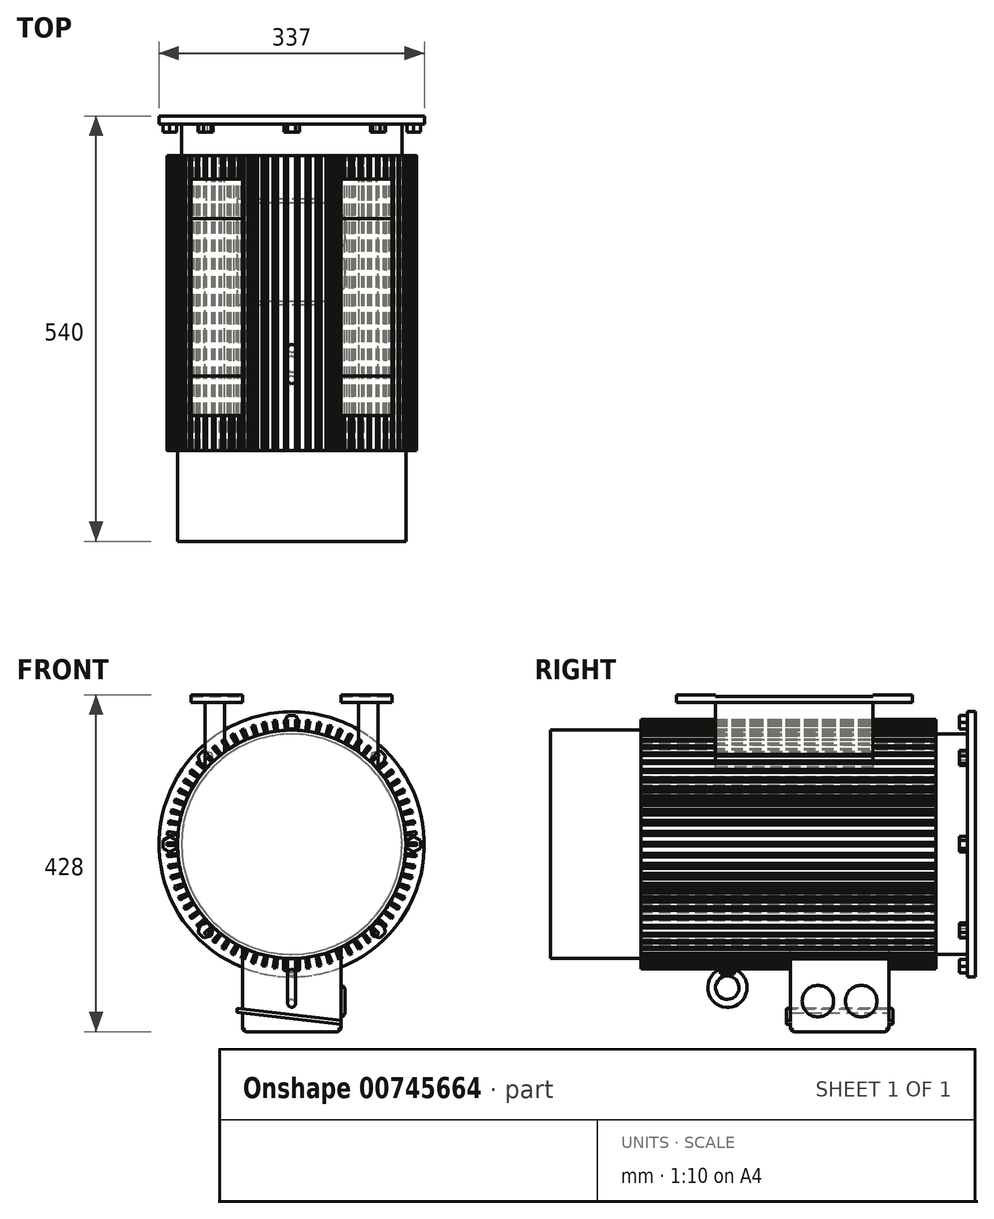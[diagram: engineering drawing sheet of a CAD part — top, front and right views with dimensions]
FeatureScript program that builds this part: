
annotation { "Feature Type Name" : "Feature", "Feature Type Description" : "" }
export const myFeature = defineFeature(function(context is Context, id is Id, definition is map)
    precondition{}
    {
        {
            var Q0;
            Q0=qCreatedBy(makeId("Front.planeOp"),FACE);
            var sketch = newSketch(context, id + "F0", { "sketchPlane" : qUnion([Q0])});
            skCircle(sketch, "E0", {"center": v(0, 0) * mm, "radius": 158.5 * mm});
            skSolve(sketch);
        }
        {
            var Q0;
            Q0=makeQuery(id+"F0.imprint","IMPRINT",FACE,{"disambiguationData":[TD([[makeQuery(id+"F0.imprint","IMPRINT",EDGE,{"derivedFrom":sQuery(id+"F0.wireOp",EDGE,"E0")}),1.0]])]});
            extrude(context, id + "F1", {"entities" : qUnion([Q0]), "depth" : 500 * mm, "offsetDistance" : 25 * mm});
        }
        {
            var Q0;
            Q0=makeQuery(id+"F1.opExtrude","CAP_FACE",FACE,{"disambiguationData":[OSD([sQuery(id+"F0.wireOp",EDGE,"E0")])],"isStart":false});
            var sketch = newSketch(context, id + "F2", { "sketchPlane" : qUnion([Q0])});
            skCircle(sketch, "E1", {"center": v(0, 0) * mm, "radius": 145 * mm});
            skSolve(sketch);
        }
        {
            var Q0;
            Q0=makeQuery(id+"F2.imprint","IMPRINT",FACE,{"disambiguationData":[TD([[makeQuery(id+"F2.imprint","IMPRINT",EDGE,{"derivedFrom":sQuery(id+"F2.wireOp",EDGE,"E1")}),-1.0]])]});
            extrude(context, id + "F3", {"entities" : qUnion([Q0]), "operationType" : NewBodyOperationType.REMOVE, "oppositeDirection" : true, "depth" : 125 * mm, "offsetDistance" : 25 * mm});
        }
        {
            var Q0;
            Q0=makeQuery(id+"F1.opExtrude","CAP_FACE",FACE,{"disambiguationData":[OSD([sQuery(id+"F0.wireOp",EDGE,"E0")])],"isStart":false});
            extrude(context, id + "F4", {"entities" : qUnion([Q0]), "operationType" : NewBodyOperationType.REMOVE, "oppositeDirection" : true, "depth" : 10 * mm, "offsetDistance" : 25 * mm});
        }
        {
            var Q0;
            Q0=makeQuery(id+"F1.opExtrude","CAP_FACE",FACE,{"disambiguationData":[OSD([sQuery(id+"F0.wireOp",EDGE,"E0")])],"isStart":true});
            var sketch = newSketch(context, id + "F5", { "sketchPlane" : qUnion([Q0])});
            skLineSegment(sketch, "E2.bottom", {"start": v(-5, 175) * mm, "end": v(5, 175) * mm});
            skLineSegment(sketch, "E2.top", {"start": v(-5, 145) * mm, "end": v(5, 145) * mm});
            skLineSegment(sketch, "E2.left", {"start": v(-5, 175) * mm, "end": v(-5, 145) * mm});
            skLineSegment(sketch, "E2.right", {"start": v(5, 175) * mm, "end": v(5, 145) * mm});
            skLineSegment(sketch, "E3.1.0", {"start": v(-10.7, 174.74) * mm, "end": v(-8.02, 144.86) * mm});
            skLineSegment(sketch, "E3.1.1", {"start": v(-20.67, 173.85) * mm, "end": v(-17.98, 143.97) * mm});
            skLineSegment(sketch, "E3.1.2", {"start": v(-17.98, 143.97) * mm, "end": v(-8.02, 144.86) * mm});
            skLineSegment(sketch, "E3.1.3", {"start": v(-20.67, 173.85) * mm, "end": v(-10.7, 174.74) * mm});
            skLineSegment(sketch, "E3.2.0", {"start": v(-26.33, 173.08) * mm, "end": v(-20.97, 143.56) * mm});
            skLineSegment(sketch, "E3.2.1", {"start": v(-36.17, 171.3) * mm, "end": v(-30.81, 141.78) * mm});
            skLineSegment(sketch, "E3.2.2", {"start": v(-30.81, 141.78) * mm, "end": v(-20.97, 143.56) * mm});
            skLineSegment(sketch, "E3.2.3", {"start": v(-36.17, 171.3) * mm, "end": v(-26.33, 173.08) * mm});
            skLineSegment(sketch, "E3.3.0", {"start": v(-41.74, 170.02) * mm, "end": v(-33.76, 141.1) * mm});
            skLineSegment(sketch, "E3.3.1", {"start": v(-51.38, 167.36) * mm, "end": v(-43.4, 138.44) * mm});
            skLineSegment(sketch, "E3.3.2", {"start": v(-43.4, 138.44) * mm, "end": v(-33.76, 141.1) * mm});
            skLineSegment(sketch, "E3.3.3", {"start": v(-51.38, 167.36) * mm, "end": v(-41.74, 170.02) * mm});
            skLineSegment(sketch, "E3.4.0", {"start": v(-56.8, 165.6) * mm, "end": v(-46.27, 137.51) * mm});
            skLineSegment(sketch, "E3.4.1", {"start": v(-66.17, 162.08) * mm, "end": v(-55.63, 134) * mm});
            skLineSegment(sketch, "E3.4.2", {"start": v(-55.63, 134) * mm, "end": v(-46.27, 137.51) * mm});
            skLineSegment(sketch, "E3.4.3", {"start": v(-66.17, 162.08) * mm, "end": v(-56.8, 165.6) * mm});
            skLineSegment(sketch, "E3.5.0", {"start": v(-71.42, 159.84) * mm, "end": v(-58.4, 132.8) * mm});
            skLineSegment(sketch, "E3.5.1", {"start": v(-80.43, 155.5) * mm, "end": v(-67.42, 128.47) * mm});
            skLineSegment(sketch, "E3.5.2", {"start": v(-67.42, 128.47) * mm, "end": v(-58.4, 132.8) * mm});
            skLineSegment(sketch, "E3.5.3", {"start": v(-80.43, 155.5) * mm, "end": v(-71.42, 159.84) * mm});
            skLineSegment(sketch, "E3.6.0", {"start": v(-85.47, 152.8) * mm, "end": v(-70.08, 127.04) * mm});
            skLineSegment(sketch, "E3.6.1", {"start": v(-94.05, 147.66) * mm, "end": v(-78.66, 121.91) * mm});
            skLineSegment(sketch, "E3.6.2", {"start": v(-78.66, 121.91) * mm, "end": v(-70.08, 127.04) * mm});
            skLineSegment(sketch, "E3.6.3", {"start": v(-94.05, 147.66) * mm, "end": v(-85.47, 152.8) * mm});
            skLineSegment(sketch, "E3.7.0", {"start": v(-98.82, 144.52) * mm, "end": v(-81.18, 120.25) * mm});
            skLineSegment(sketch, "E3.7.1", {"start": v(-106.9, 138.64) * mm, "end": v(-89.27, 114.37) * mm});
            skLineSegment(sketch, "E3.7.2", {"start": v(-89.27, 114.37) * mm, "end": v(-81.18, 120.25) * mm});
            skLineSegment(sketch, "E3.7.3", {"start": v(-106.9, 138.64) * mm, "end": v(-98.82, 144.52) * mm});
            skLineSegment(sketch, "E3.8.0", {"start": v(-111.37, 135.08) * mm, "end": v(-91.64, 112.49) * mm});
            skLineSegment(sketch, "E3.8.1", {"start": v(-118.9, 128.5) * mm, "end": v(-99.17, 105.9) * mm});
            skLineSegment(sketch, "E3.8.2", {"start": v(-99.17, 105.9) * mm, "end": v(-91.64, 112.49) * mm});
            skLineSegment(sketch, "E3.8.3", {"start": v(-118.9, 128.5) * mm, "end": v(-111.37, 135.08) * mm});
            skLineSegment(sketch, "E3.9.0", {"start": v(-123.03, 124.55) * mm, "end": v(-101.35, 103.82) * mm});
            skLineSegment(sketch, "E3.9.1", {"start": v(-129.94, 117.32) * mm, "end": v(-108.26, 96.6) * mm});
            skLineSegment(sketch, "E3.9.2", {"start": v(-108.26, 96.6) * mm, "end": v(-101.35, 103.82) * mm});
            skLineSegment(sketch, "E3.9.3", {"start": v(-129.94, 117.32) * mm, "end": v(-123.03, 124.55) * mm});
            skLineSegment(sketch, "E3.10.0", {"start": v(-133.7, 113.02) * mm, "end": v(-110.25, 94.32) * mm});
            skLineSegment(sketch, "E3.10.1", {"start": v(-139.94, 105.2) * mm, "end": v(-116.48, 86.5) * mm});
            skLineSegment(sketch, "E3.10.2", {"start": v(-116.48, 86.5) * mm, "end": v(-110.25, 94.32) * mm});
            skLineSegment(sketch, "E3.10.3", {"start": v(-139.94, 105.2) * mm, "end": v(-133.7, 113.02) * mm});
            skLineSegment(sketch, "E3.11.0", {"start": v(-143.3, 100.58) * mm, "end": v(-118.26, 84.05) * mm});
            skLineSegment(sketch, "E3.11.1", {"start": v(-148.8, 92.23) * mm, "end": v(-123.77, 75.7) * mm});
            skLineSegment(sketch, "E3.11.2", {"start": v(-123.77, 75.7) * mm, "end": v(-118.26, 84.05) * mm});
            skLineSegment(sketch, "E3.11.3", {"start": v(-148.8, 92.23) * mm, "end": v(-143.3, 100.58) * mm});
            skLineSegment(sketch, "E3.12.0", {"start": v(-151.73, 87.33) * mm, "end": v(-125.32, 73.11) * mm});
            skLineSegment(sketch, "E3.12.1", {"start": v(-156.47, 78.52) * mm, "end": v(-130.06, 64.3) * mm});
            skLineSegment(sketch, "E3.12.2", {"start": v(-130.06, 64.3) * mm, "end": v(-125.32, 73.11) * mm});
            skLineSegment(sketch, "E3.12.3", {"start": v(-156.47, 78.52) * mm, "end": v(-151.73, 87.33) * mm});
            skLineSegment(sketch, "E3.13.0", {"start": v(-158.95, 73.38) * mm, "end": v(-131.37, 61.59) * mm});
            skLineSegment(sketch, "E3.13.1", {"start": v(-162.88, 64.18) * mm, "end": v(-135.3, 52.4) * mm});
            skLineSegment(sketch, "E3.13.2", {"start": v(-135.3, 52.4) * mm, "end": v(-131.37, 61.59) * mm});
            skLineSegment(sketch, "E3.13.3", {"start": v(-162.88, 64.18) * mm, "end": v(-158.95, 73.38) * mm});
            skLineSegment(sketch, "E3.14.0", {"start": v(-164.89, 58.83) * mm, "end": v(-136.36, 49.56) * mm});
            skLineSegment(sketch, "E3.14.1", {"start": v(-167.98, 49.32) * mm, "end": v(-139.45, 40.05) * mm});
            skLineSegment(sketch, "E3.14.2", {"start": v(-139.45, 40.05) * mm, "end": v(-136.36, 49.56) * mm});
            skLineSegment(sketch, "E3.14.3", {"start": v(-167.98, 49.32) * mm, "end": v(-164.89, 58.83) * mm});
            skLineSegment(sketch, "E3.15.0", {"start": v(-169.5, 43.82) * mm, "end": v(-140.25, 37.14) * mm});
            skLineSegment(sketch, "E3.15.1", {"start": v(-171.72, 34.07) * mm, "end": v(-142.48, 27.4) * mm});
            skLineSegment(sketch, "E3.15.2", {"start": v(-142.48, 27.4) * mm, "end": v(-140.25, 37.14) * mm});
            skLineSegment(sketch, "E3.15.3", {"start": v(-171.72, 34.07) * mm, "end": v(-169.5, 43.82) * mm});
            skLineSegment(sketch, "E3.16.0", {"start": v(-172.75, 28.45) * mm, "end": v(-143.02, 24.42) * mm});
            skLineSegment(sketch, "E3.16.1", {"start": v(-174.09, 18.54) * mm, "end": v(-144.36, 14.5) * mm});
            skLineSegment(sketch, "E3.16.2", {"start": v(-144.36, 14.5) * mm, "end": v(-143.02, 24.42) * mm});
            skLineSegment(sketch, "E3.16.3", {"start": v(-174.09, 18.54) * mm, "end": v(-172.75, 28.45) * mm});
            skLineSegment(sketch, "E3.17.0", {"start": v(-174.6, 12.85) * mm, "end": v(-144.63, 11.5) * mm});
            skLineSegment(sketch, "E3.17.1", {"start": v(-175.05, 2.86) * mm, "end": v(-145.08, 1.51) * mm});
            skLineSegment(sketch, "E3.17.2", {"start": v(-145.08, 1.51) * mm, "end": v(-144.63, 11.5) * mm});
            skLineSegment(sketch, "E3.17.3", {"start": v(-175.05, 2.86) * mm, "end": v(-174.6, 12.85) * mm});
            skLineSegment(sketch, "E3.18.0", {"start": v(-175.05, -2.86) * mm, "end": v(-145.08, -1.51) * mm});
            skLineSegment(sketch, "E3.18.1", {"start": v(-174.6, -12.85) * mm, "end": v(-144.63, -11.5) * mm});
            skLineSegment(sketch, "E3.18.2", {"start": v(-144.63, -11.5) * mm, "end": v(-145.08, -1.51) * mm});
            skLineSegment(sketch, "E3.18.3", {"start": v(-174.6, -12.85) * mm, "end": v(-175.05, -2.86) * mm});
            skLineSegment(sketch, "E3.19.0", {"start": v(-174.09, -18.54) * mm, "end": v(-144.36, -14.5) * mm});
            skLineSegment(sketch, "E3.19.1", {"start": v(-172.75, -28.45) * mm, "end": v(-143.02, -24.42) * mm});
            skLineSegment(sketch, "E3.19.2", {"start": v(-143.02, -24.42) * mm, "end": v(-144.36, -14.5) * mm});
            skLineSegment(sketch, "E3.19.3", {"start": v(-172.75, -28.45) * mm, "end": v(-174.09, -18.54) * mm});
            skLineSegment(sketch, "E3.20.0", {"start": v(-171.72, -34.07) * mm, "end": v(-142.48, -27.4) * mm});
            skLineSegment(sketch, "E3.20.1", {"start": v(-169.5, -43.82) * mm, "end": v(-140.25, -37.14) * mm});
            skLineSegment(sketch, "E3.20.2", {"start": v(-140.25, -37.14) * mm, "end": v(-142.48, -27.4) * mm});
            skLineSegment(sketch, "E3.20.3", {"start": v(-169.5, -43.82) * mm, "end": v(-171.72, -34.07) * mm});
            skLineSegment(sketch, "E3.21.0", {"start": v(-167.98, -49.32) * mm, "end": v(-139.45, -40.05) * mm});
            skLineSegment(sketch, "E3.21.1", {"start": v(-164.89, -58.83) * mm, "end": v(-136.36, -49.56) * mm});
            skLineSegment(sketch, "E3.21.2", {"start": v(-136.36, -49.56) * mm, "end": v(-139.45, -40.05) * mm});
            skLineSegment(sketch, "E3.21.3", {"start": v(-164.89, -58.83) * mm, "end": v(-167.98, -49.32) * mm});
            skLineSegment(sketch, "E3.22.0", {"start": v(-162.88, -64.18) * mm, "end": v(-135.3, -52.4) * mm});
            skLineSegment(sketch, "E3.22.1", {"start": v(-158.95, -73.38) * mm, "end": v(-131.37, -61.59) * mm});
            skLineSegment(sketch, "E3.22.2", {"start": v(-131.37, -61.59) * mm, "end": v(-135.3, -52.4) * mm});
            skLineSegment(sketch, "E3.22.3", {"start": v(-158.95, -73.38) * mm, "end": v(-162.88, -64.18) * mm});
            skLineSegment(sketch, "E3.23.0", {"start": v(-156.47, -78.52) * mm, "end": v(-130.06, -64.3) * mm});
            skLineSegment(sketch, "E3.23.1", {"start": v(-151.73, -87.33) * mm, "end": v(-125.32, -73.11) * mm});
            skLineSegment(sketch, "E3.23.2", {"start": v(-125.32, -73.11) * mm, "end": v(-130.06, -64.3) * mm});
            skLineSegment(sketch, "E3.23.3", {"start": v(-151.73, -87.33) * mm, "end": v(-156.47, -78.52) * mm});
            skLineSegment(sketch, "E3.24.0", {"start": v(-148.8, -92.23) * mm, "end": v(-123.77, -75.7) * mm});
            skLineSegment(sketch, "E3.24.1", {"start": v(-143.3, -100.58) * mm, "end": v(-118.26, -84.05) * mm});
            skLineSegment(sketch, "E3.24.2", {"start": v(-118.26, -84.05) * mm, "end": v(-123.77, -75.7) * mm});
            skLineSegment(sketch, "E3.24.3", {"start": v(-143.3, -100.58) * mm, "end": v(-148.8, -92.23) * mm});
            skLineSegment(sketch, "E3.25.0", {"start": v(-139.94, -105.2) * mm, "end": v(-116.48, -86.5) * mm});
            skLineSegment(sketch, "E3.25.1", {"start": v(-133.7, -113.02) * mm, "end": v(-110.25, -94.32) * mm});
            skLineSegment(sketch, "E3.25.2", {"start": v(-110.25, -94.32) * mm, "end": v(-116.48, -86.5) * mm});
            skLineSegment(sketch, "E3.25.3", {"start": v(-133.7, -113.02) * mm, "end": v(-139.94, -105.2) * mm});
            skLineSegment(sketch, "E3.26.0", {"start": v(-129.94, -117.32) * mm, "end": v(-108.26, -96.6) * mm});
            skLineSegment(sketch, "E3.26.1", {"start": v(-123.03, -124.55) * mm, "end": v(-101.35, -103.82) * mm});
            skLineSegment(sketch, "E3.26.2", {"start": v(-101.35, -103.82) * mm, "end": v(-108.26, -96.6) * mm});
            skLineSegment(sketch, "E3.26.3", {"start": v(-123.03, -124.55) * mm, "end": v(-129.94, -117.32) * mm});
            skLineSegment(sketch, "E3.27.0", {"start": v(-118.9, -128.5) * mm, "end": v(-99.17, -105.9) * mm});
            skLineSegment(sketch, "E3.27.1", {"start": v(-111.37, -135.08) * mm, "end": v(-91.64, -112.49) * mm});
            skLineSegment(sketch, "E3.27.2", {"start": v(-91.64, -112.49) * mm, "end": v(-99.17, -105.9) * mm});
            skLineSegment(sketch, "E3.27.3", {"start": v(-111.37, -135.08) * mm, "end": v(-118.9, -128.5) * mm});
            skLineSegment(sketch, "E3.28.0", {"start": v(-106.9, -138.64) * mm, "end": v(-89.27, -114.37) * mm});
            skLineSegment(sketch, "E3.28.1", {"start": v(-98.82, -144.52) * mm, "end": v(-81.18, -120.25) * mm});
            skLineSegment(sketch, "E3.28.2", {"start": v(-81.18, -120.25) * mm, "end": v(-89.27, -114.37) * mm});
            skLineSegment(sketch, "E3.28.3", {"start": v(-98.82, -144.52) * mm, "end": v(-106.9, -138.64) * mm});
            skLineSegment(sketch, "E3.29.0", {"start": v(-94.05, -147.66) * mm, "end": v(-78.66, -121.91) * mm});
            skLineSegment(sketch, "E3.29.1", {"start": v(-85.47, -152.8) * mm, "end": v(-70.08, -127.04) * mm});
            skLineSegment(sketch, "E3.29.2", {"start": v(-70.08, -127.04) * mm, "end": v(-78.66, -121.91) * mm});
            skLineSegment(sketch, "E3.29.3", {"start": v(-85.47, -152.8) * mm, "end": v(-94.05, -147.66) * mm});
            skLineSegment(sketch, "E3.30.0", {"start": v(-80.43, -155.5) * mm, "end": v(-67.42, -128.47) * mm});
            skLineSegment(sketch, "E3.30.1", {"start": v(-71.42, -159.84) * mm, "end": v(-58.4, -132.8) * mm});
            skLineSegment(sketch, "E3.30.2", {"start": v(-58.4, -132.8) * mm, "end": v(-67.42, -128.47) * mm});
            skLineSegment(sketch, "E3.30.3", {"start": v(-71.42, -159.84) * mm, "end": v(-80.43, -155.5) * mm});
            skLineSegment(sketch, "E3.31.0", {"start": v(-66.17, -162.08) * mm, "end": v(-55.63, -134) * mm});
            skLineSegment(sketch, "E3.31.1", {"start": v(-56.8, -165.6) * mm, "end": v(-46.27, -137.51) * mm});
            skLineSegment(sketch, "E3.31.2", {"start": v(-46.27, -137.51) * mm, "end": v(-55.63, -134) * mm});
            skLineSegment(sketch, "E3.31.3", {"start": v(-56.8, -165.6) * mm, "end": v(-66.17, -162.08) * mm});
            skLineSegment(sketch, "E3.32.0", {"start": v(-51.38, -167.36) * mm, "end": v(-43.4, -138.44) * mm});
            skLineSegment(sketch, "E3.32.1", {"start": v(-41.74, -170.02) * mm, "end": v(-33.76, -141.1) * mm});
            skLineSegment(sketch, "E3.32.2", {"start": v(-33.76, -141.1) * mm, "end": v(-43.4, -138.44) * mm});
            skLineSegment(sketch, "E3.32.3", {"start": v(-41.74, -170.02) * mm, "end": v(-51.38, -167.36) * mm});
            skLineSegment(sketch, "E3.33.0", {"start": v(-36.17, -171.3) * mm, "end": v(-30.81, -141.78) * mm});
            skLineSegment(sketch, "E3.33.1", {"start": v(-26.33, -173.08) * mm, "end": v(-20.97, -143.56) * mm});
            skLineSegment(sketch, "E3.33.2", {"start": v(-20.97, -143.56) * mm, "end": v(-30.81, -141.78) * mm});
            skLineSegment(sketch, "E3.33.3", {"start": v(-26.33, -173.08) * mm, "end": v(-36.17, -171.3) * mm});
            skLineSegment(sketch, "E3.34.0", {"start": v(-20.67, -173.85) * mm, "end": v(-17.98, -143.97) * mm});
            skLineSegment(sketch, "E3.34.1", {"start": v(-10.7, -174.74) * mm, "end": v(-8.02, -144.86) * mm});
            skLineSegment(sketch, "E3.34.2", {"start": v(-8.02, -144.86) * mm, "end": v(-17.98, -143.97) * mm});
            skLineSegment(sketch, "E3.34.3", {"start": v(-10.7, -174.74) * mm, "end": v(-20.67, -173.85) * mm});
            skLineSegment(sketch, "E3.35.0", {"start": v(-5, -175) * mm, "end": v(-5, -145) * mm});
            skLineSegment(sketch, "E3.35.1", {"start": v(5, -175) * mm, "end": v(5, -145) * mm});
            skLineSegment(sketch, "E3.35.2", {"start": v(5, -145) * mm, "end": v(-5, -145) * mm});
            skLineSegment(sketch, "E3.35.3", {"start": v(5, -175) * mm, "end": v(-5, -175) * mm});
            skLineSegment(sketch, "E3.36.0", {"start": v(10.7, -174.74) * mm, "end": v(8.02, -144.86) * mm});
            skLineSegment(sketch, "E3.36.1", {"start": v(20.67, -173.85) * mm, "end": v(17.98, -143.97) * mm});
            skLineSegment(sketch, "E3.36.2", {"start": v(17.98, -143.97) * mm, "end": v(8.02, -144.86) * mm});
            skLineSegment(sketch, "E3.36.3", {"start": v(20.67, -173.85) * mm, "end": v(10.7, -174.74) * mm});
            skLineSegment(sketch, "E3.37.0", {"start": v(26.33, -173.08) * mm, "end": v(20.97, -143.56) * mm});
            skLineSegment(sketch, "E3.37.1", {"start": v(36.17, -171.3) * mm, "end": v(30.81, -141.78) * mm});
            skLineSegment(sketch, "E3.37.2", {"start": v(30.81, -141.78) * mm, "end": v(20.97, -143.56) * mm});
            skLineSegment(sketch, "E3.37.3", {"start": v(36.17, -171.3) * mm, "end": v(26.33, -173.08) * mm});
            skLineSegment(sketch, "E3.38.0", {"start": v(41.74, -170.02) * mm, "end": v(33.76, -141.1) * mm});
            skLineSegment(sketch, "E3.38.1", {"start": v(51.38, -167.36) * mm, "end": v(43.4, -138.44) * mm});
            skLineSegment(sketch, "E3.38.2", {"start": v(43.4, -138.44) * mm, "end": v(33.76, -141.1) * mm});
            skLineSegment(sketch, "E3.38.3", {"start": v(51.38, -167.36) * mm, "end": v(41.74, -170.02) * mm});
            skLineSegment(sketch, "E3.39.0", {"start": v(56.8, -165.6) * mm, "end": v(46.27, -137.51) * mm});
            skLineSegment(sketch, "E3.39.1", {"start": v(66.17, -162.08) * mm, "end": v(55.63, -134) * mm});
            skLineSegment(sketch, "E3.39.2", {"start": v(55.63, -134) * mm, "end": v(46.27, -137.51) * mm});
            skLineSegment(sketch, "E3.39.3", {"start": v(66.17, -162.08) * mm, "end": v(56.8, -165.6) * mm});
            skLineSegment(sketch, "E3.40.0", {"start": v(71.42, -159.84) * mm, "end": v(58.4, -132.8) * mm});
            skLineSegment(sketch, "E3.40.1", {"start": v(80.43, -155.5) * mm, "end": v(67.42, -128.47) * mm});
            skLineSegment(sketch, "E3.40.2", {"start": v(67.42, -128.47) * mm, "end": v(58.4, -132.8) * mm});
            skLineSegment(sketch, "E3.40.3", {"start": v(80.43, -155.5) * mm, "end": v(71.42, -159.84) * mm});
            skLineSegment(sketch, "E3.41.0", {"start": v(85.47, -152.8) * mm, "end": v(70.08, -127.04) * mm});
            skLineSegment(sketch, "E3.41.1", {"start": v(94.05, -147.66) * mm, "end": v(78.66, -121.91) * mm});
            skLineSegment(sketch, "E3.41.2", {"start": v(78.66, -121.91) * mm, "end": v(70.08, -127.04) * mm});
            skLineSegment(sketch, "E3.41.3", {"start": v(94.05, -147.66) * mm, "end": v(85.47, -152.8) * mm});
            skLineSegment(sketch, "E3.42.0", {"start": v(98.82, -144.52) * mm, "end": v(81.18, -120.25) * mm});
            skLineSegment(sketch, "E3.42.1", {"start": v(106.9, -138.64) * mm, "end": v(89.27, -114.37) * mm});
            skLineSegment(sketch, "E3.42.2", {"start": v(89.27, -114.37) * mm, "end": v(81.18, -120.25) * mm});
            skLineSegment(sketch, "E3.42.3", {"start": v(106.9, -138.64) * mm, "end": v(98.82, -144.52) * mm});
            skLineSegment(sketch, "E3.43.0", {"start": v(111.37, -135.08) * mm, "end": v(91.64, -112.49) * mm});
            skLineSegment(sketch, "E3.43.1", {"start": v(118.9, -128.5) * mm, "end": v(99.17, -105.9) * mm});
            skLineSegment(sketch, "E3.43.2", {"start": v(99.17, -105.9) * mm, "end": v(91.64, -112.49) * mm});
            skLineSegment(sketch, "E3.43.3", {"start": v(118.9, -128.5) * mm, "end": v(111.37, -135.08) * mm});
            skLineSegment(sketch, "E3.44.0", {"start": v(123.03, -124.55) * mm, "end": v(101.35, -103.82) * mm});
            skLineSegment(sketch, "E3.44.1", {"start": v(129.94, -117.32) * mm, "end": v(108.26, -96.6) * mm});
            skLineSegment(sketch, "E3.44.2", {"start": v(108.26, -96.6) * mm, "end": v(101.35, -103.82) * mm});
            skLineSegment(sketch, "E3.44.3", {"start": v(129.94, -117.32) * mm, "end": v(123.03, -124.55) * mm});
            skLineSegment(sketch, "E3.45.0", {"start": v(133.7, -113.02) * mm, "end": v(110.25, -94.32) * mm});
            skLineSegment(sketch, "E3.45.1", {"start": v(139.94, -105.2) * mm, "end": v(116.48, -86.5) * mm});
            skLineSegment(sketch, "E3.45.2", {"start": v(116.48, -86.5) * mm, "end": v(110.25, -94.32) * mm});
            skLineSegment(sketch, "E3.45.3", {"start": v(139.94, -105.2) * mm, "end": v(133.7, -113.02) * mm});
            skLineSegment(sketch, "E3.46.0", {"start": v(143.3, -100.58) * mm, "end": v(118.26, -84.05) * mm});
            skLineSegment(sketch, "E3.46.1", {"start": v(148.8, -92.23) * mm, "end": v(123.77, -75.7) * mm});
            skLineSegment(sketch, "E3.46.2", {"start": v(123.77, -75.7) * mm, "end": v(118.26, -84.05) * mm});
            skLineSegment(sketch, "E3.46.3", {"start": v(148.8, -92.23) * mm, "end": v(143.3, -100.58) * mm});
            skLineSegment(sketch, "E3.47.0", {"start": v(151.73, -87.33) * mm, "end": v(125.32, -73.11) * mm});
            skLineSegment(sketch, "E3.47.1", {"start": v(156.47, -78.52) * mm, "end": v(130.06, -64.3) * mm});
            skLineSegment(sketch, "E3.47.2", {"start": v(130.06, -64.3) * mm, "end": v(125.32, -73.11) * mm});
            skLineSegment(sketch, "E3.47.3", {"start": v(156.47, -78.52) * mm, "end": v(151.73, -87.33) * mm});
            skLineSegment(sketch, "E3.48.0", {"start": v(158.95, -73.38) * mm, "end": v(131.37, -61.59) * mm});
            skLineSegment(sketch, "E3.48.1", {"start": v(162.88, -64.18) * mm, "end": v(135.3, -52.4) * mm});
            skLineSegment(sketch, "E3.48.2", {"start": v(135.3, -52.4) * mm, "end": v(131.37, -61.59) * mm});
            skLineSegment(sketch, "E3.48.3", {"start": v(162.88, -64.18) * mm, "end": v(158.95, -73.38) * mm});
            skLineSegment(sketch, "E3.49.0", {"start": v(164.89, -58.83) * mm, "end": v(136.36, -49.56) * mm});
            skLineSegment(sketch, "E3.49.1", {"start": v(167.98, -49.32) * mm, "end": v(139.45, -40.05) * mm});
            skLineSegment(sketch, "E3.49.2", {"start": v(139.45, -40.05) * mm, "end": v(136.36, -49.56) * mm});
            skLineSegment(sketch, "E3.49.3", {"start": v(167.98, -49.32) * mm, "end": v(164.89, -58.83) * mm});
            skLineSegment(sketch, "E3.50.0", {"start": v(169.5, -43.82) * mm, "end": v(140.25, -37.14) * mm});
            skLineSegment(sketch, "E3.50.1", {"start": v(171.72, -34.07) * mm, "end": v(142.48, -27.4) * mm});
            skLineSegment(sketch, "E3.50.2", {"start": v(142.48, -27.4) * mm, "end": v(140.25, -37.14) * mm});
            skLineSegment(sketch, "E3.50.3", {"start": v(171.72, -34.07) * mm, "end": v(169.5, -43.82) * mm});
            skLineSegment(sketch, "E3.51.0", {"start": v(172.75, -28.45) * mm, "end": v(143.02, -24.42) * mm});
            skLineSegment(sketch, "E3.51.1", {"start": v(174.09, -18.54) * mm, "end": v(144.36, -14.5) * mm});
            skLineSegment(sketch, "E3.51.2", {"start": v(144.36, -14.5) * mm, "end": v(143.02, -24.42) * mm});
            skLineSegment(sketch, "E3.51.3", {"start": v(174.09, -18.54) * mm, "end": v(172.75, -28.45) * mm});
            skLineSegment(sketch, "E3.52.0", {"start": v(174.6, -12.85) * mm, "end": v(144.63, -11.5) * mm});
            skLineSegment(sketch, "E3.52.1", {"start": v(175.05, -2.86) * mm, "end": v(145.08, -1.51) * mm});
            skLineSegment(sketch, "E3.52.2", {"start": v(145.08, -1.51) * mm, "end": v(144.63, -11.5) * mm});
            skLineSegment(sketch, "E3.52.3", {"start": v(175.05, -2.86) * mm, "end": v(174.6, -12.85) * mm});
            skLineSegment(sketch, "E3.53.0", {"start": v(175.05, 2.86) * mm, "end": v(145.08, 1.51) * mm});
            skLineSegment(sketch, "E3.53.1", {"start": v(174.6, 12.85) * mm, "end": v(144.63, 11.5) * mm});
            skLineSegment(sketch, "E3.53.2", {"start": v(144.63, 11.5) * mm, "end": v(145.08, 1.51) * mm});
            skLineSegment(sketch, "E3.53.3", {"start": v(174.6, 12.85) * mm, "end": v(175.05, 2.86) * mm});
            skLineSegment(sketch, "E3.54.0", {"start": v(174.09, 18.54) * mm, "end": v(144.36, 14.5) * mm});
            skLineSegment(sketch, "E3.54.1", {"start": v(172.75, 28.45) * mm, "end": v(143.02, 24.42) * mm});
            skLineSegment(sketch, "E3.54.2", {"start": v(143.02, 24.42) * mm, "end": v(144.36, 14.5) * mm});
            skLineSegment(sketch, "E3.54.3", {"start": v(172.75, 28.45) * mm, "end": v(174.09, 18.54) * mm});
            skLineSegment(sketch, "E3.55.0", {"start": v(171.72, 34.07) * mm, "end": v(142.48, 27.4) * mm});
            skLineSegment(sketch, "E3.55.1", {"start": v(169.5, 43.82) * mm, "end": v(140.25, 37.14) * mm});
            skLineSegment(sketch, "E3.55.2", {"start": v(140.25, 37.14) * mm, "end": v(142.48, 27.4) * mm});
            skLineSegment(sketch, "E3.55.3", {"start": v(169.5, 43.82) * mm, "end": v(171.72, 34.07) * mm});
            skLineSegment(sketch, "E3.56.0", {"start": v(167.98, 49.32) * mm, "end": v(139.45, 40.05) * mm});
            skLineSegment(sketch, "E3.56.1", {"start": v(164.89, 58.83) * mm, "end": v(136.36, 49.56) * mm});
            skLineSegment(sketch, "E3.56.2", {"start": v(136.36, 49.56) * mm, "end": v(139.45, 40.05) * mm});
            skLineSegment(sketch, "E3.56.3", {"start": v(164.89, 58.83) * mm, "end": v(167.98, 49.32) * mm});
            skLineSegment(sketch, "E3.57.0", {"start": v(162.88, 64.18) * mm, "end": v(135.3, 52.4) * mm});
            skLineSegment(sketch, "E3.57.1", {"start": v(158.95, 73.38) * mm, "end": v(131.37, 61.59) * mm});
            skLineSegment(sketch, "E3.57.2", {"start": v(131.37, 61.59) * mm, "end": v(135.3, 52.4) * mm});
            skLineSegment(sketch, "E3.57.3", {"start": v(158.95, 73.38) * mm, "end": v(162.88, 64.18) * mm});
            skLineSegment(sketch, "E3.58.0", {"start": v(156.47, 78.52) * mm, "end": v(130.06, 64.3) * mm});
            skLineSegment(sketch, "E3.58.1", {"start": v(151.73, 87.33) * mm, "end": v(125.32, 73.11) * mm});
            skLineSegment(sketch, "E3.58.2", {"start": v(125.32, 73.11) * mm, "end": v(130.06, 64.3) * mm});
            skLineSegment(sketch, "E3.58.3", {"start": v(151.73, 87.33) * mm, "end": v(156.47, 78.52) * mm});
            skLineSegment(sketch, "E3.59.0", {"start": v(148.8, 92.23) * mm, "end": v(123.77, 75.7) * mm});
            skLineSegment(sketch, "E3.59.1", {"start": v(143.3, 100.58) * mm, "end": v(118.26, 84.05) * mm});
            skLineSegment(sketch, "E3.59.2", {"start": v(118.26, 84.05) * mm, "end": v(123.77, 75.7) * mm});
            skLineSegment(sketch, "E3.59.3", {"start": v(143.3, 100.58) * mm, "end": v(148.8, 92.23) * mm});
            skLineSegment(sketch, "E3.60.0", {"start": v(139.94, 105.2) * mm, "end": v(116.48, 86.5) * mm});
            skLineSegment(sketch, "E3.60.1", {"start": v(133.7, 113.02) * mm, "end": v(110.25, 94.32) * mm});
            skLineSegment(sketch, "E3.60.2", {"start": v(110.25, 94.32) * mm, "end": v(116.48, 86.5) * mm});
            skLineSegment(sketch, "E3.60.3", {"start": v(133.7, 113.02) * mm, "end": v(139.94, 105.2) * mm});
            skLineSegment(sketch, "E3.61.0", {"start": v(129.94, 117.32) * mm, "end": v(108.26, 96.6) * mm});
            skLineSegment(sketch, "E3.61.1", {"start": v(123.03, 124.55) * mm, "end": v(101.35, 103.82) * mm});
            skLineSegment(sketch, "E3.61.2", {"start": v(101.35, 103.82) * mm, "end": v(108.26, 96.6) * mm});
            skLineSegment(sketch, "E3.61.3", {"start": v(123.03, 124.55) * mm, "end": v(129.94, 117.32) * mm});
            skLineSegment(sketch, "E3.62.0", {"start": v(118.9, 128.5) * mm, "end": v(99.17, 105.9) * mm});
            skLineSegment(sketch, "E3.62.1", {"start": v(111.37, 135.08) * mm, "end": v(91.64, 112.49) * mm});
            skLineSegment(sketch, "E3.62.2", {"start": v(91.64, 112.49) * mm, "end": v(99.17, 105.9) * mm});
            skLineSegment(sketch, "E3.62.3", {"start": v(111.37, 135.08) * mm, "end": v(118.9, 128.5) * mm});
            skLineSegment(sketch, "E3.63.0", {"start": v(106.9, 138.64) * mm, "end": v(89.27, 114.37) * mm});
            skLineSegment(sketch, "E3.63.1", {"start": v(98.82, 144.52) * mm, "end": v(81.18, 120.25) * mm});
            skLineSegment(sketch, "E3.63.2", {"start": v(81.18, 120.25) * mm, "end": v(89.27, 114.37) * mm});
            skLineSegment(sketch, "E3.63.3", {"start": v(98.82, 144.52) * mm, "end": v(106.9, 138.64) * mm});
            skLineSegment(sketch, "E3.64.0", {"start": v(94.05, 147.66) * mm, "end": v(78.66, 121.91) * mm});
            skLineSegment(sketch, "E3.64.1", {"start": v(85.47, 152.8) * mm, "end": v(70.08, 127.04) * mm});
            skLineSegment(sketch, "E3.64.2", {"start": v(70.08, 127.04) * mm, "end": v(78.66, 121.91) * mm});
            skLineSegment(sketch, "E3.64.3", {"start": v(85.47, 152.8) * mm, "end": v(94.05, 147.66) * mm});
            skLineSegment(sketch, "E3.65.0", {"start": v(80.43, 155.5) * mm, "end": v(67.42, 128.47) * mm});
            skLineSegment(sketch, "E3.65.1", {"start": v(71.42, 159.84) * mm, "end": v(58.4, 132.8) * mm});
            skLineSegment(sketch, "E3.65.2", {"start": v(58.4, 132.8) * mm, "end": v(67.42, 128.47) * mm});
            skLineSegment(sketch, "E3.65.3", {"start": v(71.42, 159.84) * mm, "end": v(80.43, 155.5) * mm});
            skLineSegment(sketch, "E3.66.0", {"start": v(66.17, 162.08) * mm, "end": v(55.63, 134) * mm});
            skLineSegment(sketch, "E3.66.1", {"start": v(56.8, 165.6) * mm, "end": v(46.27, 137.51) * mm});
            skLineSegment(sketch, "E3.66.2", {"start": v(46.27, 137.51) * mm, "end": v(55.63, 134) * mm});
            skLineSegment(sketch, "E3.66.3", {"start": v(56.8, 165.6) * mm, "end": v(66.17, 162.08) * mm});
            skLineSegment(sketch, "E3.67.0", {"start": v(51.38, 167.36) * mm, "end": v(43.4, 138.44) * mm});
            skLineSegment(sketch, "E3.67.1", {"start": v(41.74, 170.02) * mm, "end": v(33.76, 141.1) * mm});
            skLineSegment(sketch, "E3.67.2", {"start": v(33.76, 141.1) * mm, "end": v(43.4, 138.44) * mm});
            skLineSegment(sketch, "E3.67.3", {"start": v(41.74, 170.02) * mm, "end": v(51.38, 167.36) * mm});
            skLineSegment(sketch, "E3.68.0", {"start": v(36.17, 171.3) * mm, "end": v(30.81, 141.78) * mm});
            skLineSegment(sketch, "E3.68.1", {"start": v(26.33, 173.08) * mm, "end": v(20.97, 143.56) * mm});
            skLineSegment(sketch, "E3.68.2", {"start": v(20.97, 143.56) * mm, "end": v(30.81, 141.78) * mm});
            skLineSegment(sketch, "E3.68.3", {"start": v(26.33, 173.08) * mm, "end": v(36.17, 171.3) * mm});
            skLineSegment(sketch, "E3.69.0", {"start": v(20.67, 173.85) * mm, "end": v(17.98, 143.97) * mm});
            skLineSegment(sketch, "E3.69.1", {"start": v(10.7, 174.74) * mm, "end": v(8.02, 144.86) * mm});
            skLineSegment(sketch, "E3.69.2", {"start": v(8.02, 144.86) * mm, "end": v(17.98, 143.97) * mm});
            skLineSegment(sketch, "E3.69.3", {"start": v(10.7, 174.74) * mm, "end": v(20.67, 173.85) * mm});
            skPoint(sketch, "E3.center", {"position": v(0, 0) * mm});
            skSolve(sketch);
        }
        {
            var Q0;
            Q0 = qSketchRegion(id + "F5", true);
            extrude(context, id + "F6", {"entities" : qUnion([Q0]), "operationType" : NewBodyOperationType.REMOVE, "endBound" : BoundingType.THROUGH_ALL, "oppositeDirection" : true, "depth" : 25 * mm, "offsetDistance" : 25 * mm});
        }
        {
            var Q0;
            Q0=makeQuery(id+"F1.opExtrude","CAP_FACE",FACE,{"disambiguationData":[OSD([sQuery(id+"F0.wireOp",EDGE,"E0")])],"isStart":true});
            var sketch = newSketch(context, id + "F7", { "sketchPlane" : qUnion([Q0])});
            skCircle(sketch, "E4", {"center": v(0, 0) * mm, "radius": 140 * mm});
            skSolve(sketch);
        }
        {
            var Q0;
            Q0=makeQuery(id+"F7.imprint","IMPRINT",FACE,{"disambiguationData":[TD([[makeQuery(id+"F7.imprint","IMPRINT",EDGE,{"derivedFrom":sQuery(id+"F7.wireOp",EDGE,"E4")}),1.0]])]});
            extrude(context, id + "F8", {"entities" : qUnion([Q0]), "operationType" : NewBodyOperationType.ADD, "depth" : 40 * mm, "offsetDistance" : 25 * mm});
        }
        {
            var Q0;
            Q0=makeQuery(id+"F8.opExtrude","CAP_FACE",FACE,{"disambiguationData":[OSD([sQuery(id+"F7.wireOp",EDGE,"E4")])],"isStart":false});
            var sketch = newSketch(context, id + "F9", { "sketchPlane" : qUnion([Q0])});
            skCircle(sketch, "E5", {"center": v(0, 0) * mm, "radius": 168.5 * mm});
            skSolve(sketch);
        }
        {
            var Q0;
            Q0 = qSketchRegion(id + "F9", true);
            extrude(context, id + "F10", {"entities" : qUnion([Q0]), "operationType" : NewBodyOperationType.ADD, "depth" : 10 * mm, "offsetDistance" : 25 * mm});
        }
        {
            var Q0;
            Q0=qCreatedBy(makeId("Top.planeOp"),FACE);
            var sketch = newSketch(context, id + "F11", { "sketchPlane" : qUnion([Q0])});
            skLineSegment(sketch, "E6.bottom", {"start": v(110, -80) * mm, "end": v(85, -80) * mm});
            skLineSegment(sketch, "E6.top", {"start": v(110, -280) * mm, "end": v(85, -280) * mm});
            skLineSegment(sketch, "E6.left", {"start": v(110, -80) * mm, "end": v(110, -280) * mm});
            skLineSegment(sketch, "E6.right", {"start": v(85, -80) * mm, "end": v(85, -280) * mm});
            skLineSegment(sketch, "E7.MirrorCS", {"start": v(-110, -80) * mm, "end": v(-85, -80) * mm});
            skLineSegment(sketch, "E8.MirrorCS", {"start": v(-85, -80) * mm, "end": v(-85, -280) * mm});
            skLineSegment(sketch, "E9.MirrorCS", {"start": v(-110, -280) * mm, "end": v(-85, -280) * mm});
            skLineSegment(sketch, "E10.MirrorCS", {"start": v(-110, -80) * mm, "end": v(-110, -280) * mm});
            skSolve(sketch);
        }
        {
            var Q0;
            Q0 = qSketchRegion(id + "F11", true);
            extrude(context, id + "F12", {"entities" : qUnion([Q0]), "operationType" : NewBodyOperationType.ADD, "depth" : 180 * mm, "offsetDistance" : 25 * mm});
        }
        {
            var Q0;
            Q0=makeQuery(id+"F12.opExtrude","CAP_FACE",FACE,{"disambiguationData":[OSD([sQuery(id+"F11.wireOp",EDGE,"E6.bottom"),sQuery(id+"F11.wireOp",EDGE,"E6.top"),sQuery(id+"F11.wireOp",EDGE,"E6.left"),sQuery(id+"F11.wireOp",EDGE,"E6.right")])],"isStart":false});
            var sketch = newSketch(context, id + "F13", { "sketchPlane" : qUnion([Q0])});
            skLineSegment(sketch, "E11.bottom", {"start": v(127.5, -30) * mm, "end": v(62.5, -30) * mm});
            skLineSegment(sketch, "E11.top", {"start": v(127.5, -330) * mm, "end": v(62.5, -330) * mm});
            skLineSegment(sketch, "E11.left", {"start": v(127.5, -30) * mm, "end": v(127.5, -330) * mm});
            skLineSegment(sketch, "E11.right", {"start": v(62.5, -30) * mm, "end": v(62.5, -330) * mm});
            skLineSegment(sketch, "E12.MirrorCS", {"start": v(-127.5, -30) * mm, "end": v(-62.5, -30) * mm});
            skLineSegment(sketch, "E13.MirrorCS", {"start": v(-127.5, -330) * mm, "end": v(-62.5, -330) * mm});
            skLineSegment(sketch, "E14.MirrorCS", {"start": v(-62.5, -30) * mm, "end": v(-62.5, -330) * mm});
            skLineSegment(sketch, "E15.MirrorCS", {"start": v(-127.5, -30) * mm, "end": v(-127.5, -330) * mm});
            skSolve(sketch);
        }
        {
            var Q0;
            Q0 = qSketchRegion(id + "F13", true);
            extrude(context, id + "F14", {"entities" : qUnion([Q0]), "operationType" : NewBodyOperationType.ADD, "depth" : 10 * mm, "offsetDistance" : 25 * mm});
        }
        {
            var Q0;
            Q0=makeQuery(id+"F14.opExtrude","SWEPT_FACE",FACE,{"disambiguationData":[OSD([sQuery(id+"F13.wireOp",EDGE,"E11.left")])]});
            var sketch = newSketch(context, id + "F15", { "sketchPlane" : qUnion([Q0])});
            skLineSegment(sketch, "E16.bottom", {"start": v(-80, 190) * mm, "end": v(-280, 190) * mm});
            skLineSegment(sketch, "E16.top", {"start": v(-80, 188) * mm, "end": v(-280, 188) * mm});
            skLineSegment(sketch, "E16.left", {"start": v(-80, 190) * mm, "end": v(-80, 188) * mm});
            skLineSegment(sketch, "E16.right", {"start": v(-280, 190) * mm, "end": v(-280, 188) * mm});
            skSolve(sketch);
        }
        {
            var Q0;
            Q0 = qSketchRegion(id + "F15", true);
            extrude(context, id + "F16", {"entities" : qUnion([Q0]), "operationType" : NewBodyOperationType.REMOVE, "endBound" : BoundingType.THROUGH_ALL, "oppositeDirection" : true, "depth" : 25 * mm, "offsetDistance" : 25 * mm});
        }
        {
            var Q0;
            Q0=makeQuery(id+"F10.opExtrude","CAP_FACE",FACE,{"disambiguationData":[OSD([sQuery(id+"F9.wireOp",EDGE,"E5")])],"isStart":true});
            var sketch = newSketch(context, id + "F17", { "sketchPlane" : qUnion([Q0])});
            skCircle(sketch, "E17.cCircle", {"center": v(0, 154.97) * mm, "radius": 8.52 * mm, "construction": true});
            skLineSegment(sketch, "E17.0", {"start": v(4.92, 146.44) * mm, "end": v(-4.92, 146.44) * mm});
            skLineSegment(sketch, "E17.1", {"start": v(-4.92, 146.44) * mm, "end": v(-9.84, 154.97) * mm});
            skLineSegment(sketch, "E17.2", {"start": v(-9.84, 154.97) * mm, "end": v(-4.92, 163.49) * mm});
            skLineSegment(sketch, "E17.3", {"start": v(-4.92, 163.49) * mm, "end": v(4.92, 163.49) * mm});
            skLineSegment(sketch, "E17.4", {"start": v(4.92, 163.49) * mm, "end": v(9.84, 154.97) * mm});
            skLineSegment(sketch, "E17.5", {"start": v(9.84, 154.97) * mm, "end": v(4.92, 146.44) * mm});
            skPoint(sketch, "E17.0.midPoint", {"position": v(0, 146.44) * mm});
            skPoint(sketch, "E18.1.0", {"position": v(-103.55, 103.55) * mm});
            skLineSegment(sketch, "E18.1.1", {"start": v(-107.03, 100.07) * mm, "end": v(-116.54, 102.62) * mm});
            skLineSegment(sketch, "E18.1.2", {"start": v(-100.07, 107.03) * mm, "end": v(-107.03, 100.07) * mm});
            skLineSegment(sketch, "E18.1.3", {"start": v(-112.12, 119.08) * mm, "end": v(-102.62, 116.54) * mm});
            skLineSegment(sketch, "E18.1.4", {"start": v(-102.62, 116.54) * mm, "end": v(-100.07, 107.03) * mm});
            skLineSegment(sketch, "E18.1.5", {"start": v(-116.54, 102.62) * mm, "end": v(-119.08, 112.12) * mm});
            skLineSegment(sketch, "E18.1.6", {"start": v(-119.08, 112.12) * mm, "end": v(-112.12, 119.08) * mm});
            skCircle(sketch, "E18.1.7", {"center": v(-109.58, 109.58) * mm, "radius": 8.52 * mm, "construction": true});
            skPoint(sketch, "E18.2.0", {"position": v(-146.44, 0) * mm});
            skLineSegment(sketch, "E18.2.1", {"start": v(-146.44, -4.92) * mm, "end": v(-154.97, -9.84) * mm});
            skLineSegment(sketch, "E18.2.2", {"start": v(-146.44, 4.92) * mm, "end": v(-146.44, -4.92) * mm});
            skLineSegment(sketch, "E18.2.3", {"start": v(-163.49, 4.92) * mm, "end": v(-154.97, 9.84) * mm});
            skLineSegment(sketch, "E18.2.4", {"start": v(-154.97, 9.84) * mm, "end": v(-146.44, 4.92) * mm});
            skLineSegment(sketch, "E18.2.5", {"start": v(-154.97, -9.84) * mm, "end": v(-163.49, -4.92) * mm});
            skLineSegment(sketch, "E18.2.6", {"start": v(-163.49, -4.92) * mm, "end": v(-163.49, 4.92) * mm});
            skCircle(sketch, "E18.2.7", {"center": v(-154.97, 0) * mm, "radius": 8.52 * mm, "construction": true});
            skPoint(sketch, "E18.3.0", {"position": v(-103.55, -103.55) * mm});
            skLineSegment(sketch, "E18.3.1", {"start": v(-100.07, -107.03) * mm, "end": v(-102.62, -116.54) * mm});
            skLineSegment(sketch, "E18.3.2", {"start": v(-107.03, -100.07) * mm, "end": v(-100.07, -107.03) * mm});
            skLineSegment(sketch, "E18.3.3", {"start": v(-119.08, -112.12) * mm, "end": v(-116.54, -102.62) * mm});
            skLineSegment(sketch, "E18.3.4", {"start": v(-116.54, -102.62) * mm, "end": v(-107.03, -100.07) * mm});
            skLineSegment(sketch, "E18.3.5", {"start": v(-102.62, -116.54) * mm, "end": v(-112.12, -119.08) * mm});
            skLineSegment(sketch, "E18.3.6", {"start": v(-112.12, -119.08) * mm, "end": v(-119.08, -112.12) * mm});
            skCircle(sketch, "E18.3.7", {"center": v(-109.58, -109.58) * mm, "radius": 8.52 * mm, "construction": true});
            skPoint(sketch, "E18.4.0", {"position": v(0, -146.44) * mm});
            skLineSegment(sketch, "E18.4.1", {"start": v(4.92, -146.44) * mm, "end": v(9.84, -154.97) * mm});
            skLineSegment(sketch, "E18.4.2", {"start": v(-4.92, -146.44) * mm, "end": v(4.92, -146.44) * mm});
            skLineSegment(sketch, "E18.4.3", {"start": v(-4.92, -163.49) * mm, "end": v(-9.84, -154.97) * mm});
            skLineSegment(sketch, "E18.4.4", {"start": v(-9.84, -154.97) * mm, "end": v(-4.92, -146.44) * mm});
            skLineSegment(sketch, "E18.4.5", {"start": v(9.84, -154.97) * mm, "end": v(4.92, -163.49) * mm});
            skLineSegment(sketch, "E18.4.6", {"start": v(4.92, -163.49) * mm, "end": v(-4.92, -163.49) * mm});
            skCircle(sketch, "E18.4.7", {"center": v(0, -154.97) * mm, "radius": 8.52 * mm, "construction": true});
            skPoint(sketch, "E18.5.0", {"position": v(103.55, -103.55) * mm});
            skLineSegment(sketch, "E18.5.1", {"start": v(107.03, -100.07) * mm, "end": v(116.54, -102.62) * mm});
            skLineSegment(sketch, "E18.5.2", {"start": v(100.07, -107.03) * mm, "end": v(107.03, -100.07) * mm});
            skLineSegment(sketch, "E18.5.3", {"start": v(112.12, -119.08) * mm, "end": v(102.62, -116.54) * mm});
            skLineSegment(sketch, "E18.5.4", {"start": v(102.62, -116.54) * mm, "end": v(100.07, -107.03) * mm});
            skLineSegment(sketch, "E18.5.5", {"start": v(116.54, -102.62) * mm, "end": v(119.08, -112.12) * mm});
            skLineSegment(sketch, "E18.5.6", {"start": v(119.08, -112.12) * mm, "end": v(112.12, -119.08) * mm});
            skCircle(sketch, "E18.5.7", {"center": v(109.58, -109.58) * mm, "radius": 8.52 * mm, "construction": true});
            skPoint(sketch, "E18.6.0", {"position": v(146.44, 0) * mm});
            skLineSegment(sketch, "E18.6.1", {"start": v(146.44, 4.92) * mm, "end": v(154.97, 9.84) * mm});
            skLineSegment(sketch, "E18.6.2", {"start": v(146.44, -4.92) * mm, "end": v(146.44, 4.92) * mm});
            skLineSegment(sketch, "E18.6.3", {"start": v(163.49, -4.92) * mm, "end": v(154.97, -9.84) * mm});
            skLineSegment(sketch, "E18.6.4", {"start": v(154.97, -9.84) * mm, "end": v(146.44, -4.92) * mm});
            skLineSegment(sketch, "E18.6.5", {"start": v(154.97, 9.84) * mm, "end": v(163.49, 4.92) * mm});
            skLineSegment(sketch, "E18.6.6", {"start": v(163.49, 4.92) * mm, "end": v(163.49, -4.92) * mm});
            skCircle(sketch, "E18.6.7", {"center": v(154.97, 0) * mm, "radius": 8.52 * mm, "construction": true});
            skPoint(sketch, "E18.7.0", {"position": v(103.55, 103.55) * mm});
            skLineSegment(sketch, "E18.7.1", {"start": v(100.07, 107.03) * mm, "end": v(102.62, 116.54) * mm});
            skLineSegment(sketch, "E18.7.2", {"start": v(107.03, 100.07) * mm, "end": v(100.07, 107.03) * mm});
            skLineSegment(sketch, "E18.7.3", {"start": v(119.08, 112.12) * mm, "end": v(116.54, 102.62) * mm});
            skLineSegment(sketch, "E18.7.4", {"start": v(116.54, 102.62) * mm, "end": v(107.03, 100.07) * mm});
            skLineSegment(sketch, "E18.7.5", {"start": v(102.62, 116.54) * mm, "end": v(112.12, 119.08) * mm});
            skLineSegment(sketch, "E18.7.6", {"start": v(112.12, 119.08) * mm, "end": v(119.08, 112.12) * mm});
            skCircle(sketch, "E18.7.7", {"center": v(109.58, 109.58) * mm, "radius": 8.52 * mm, "construction": true});
            skPoint(sketch, "E18.center", {"position": v(0, 0) * mm});
            skSolve(sketch);
        }
        {
            var Q0;
            Q0 = qSketchRegion(id + "F17", true);
            extrude(context, id + "F18", {"entities" : qUnion([Q0]), "operationType" : NewBodyOperationType.ADD, "depth" : 10 * mm, "offsetDistance" : 25 * mm});
        }
        {
            var Q0;
            Q0=qCreatedBy(makeId("Top.planeOp"),FACE);
            var sketch = newSketch(context, id + "F19", { "sketchPlane" : qUnion([Q0])});
            skLineSegment(sketch, "E19.bottom", {"start": v(-62.5, -60) * mm, "end": v(62.5, -60) * mm});
            skLineSegment(sketch, "E19.top", {"start": v(-62.5, -185) * mm, "end": v(62.5, -185) * mm});
            skLineSegment(sketch, "E19.left", {"start": v(-62.5, -60) * mm, "end": v(-62.5, -185) * mm});
            skLineSegment(sketch, "E19.right", {"start": v(62.5, -60) * mm, "end": v(62.5, -185) * mm});
            skSolve(sketch);
        }
        {
            var Q0;
            Q0 = qSketchRegion(id + "F19", true);
            extrude(context, id + "F20", {"entities" : qUnion([Q0]), "operationType" : NewBodyOperationType.ADD, "oppositeDirection" : true, "depth" : 238 * mm, "offsetDistance" : 25 * mm});
        }
        {
            var Q0;
            {var subQ2=sQuery(id+"F19.wireOp",EDGE,"E19.bottom");Q0=makeQuery(id+"F20.boolean.opBoolean","SPLIT",FACE,{"disambiguationData":[TD([makeQuery(id+"F1.opExtrude","SWEPT_FACE",FACE,{"disambiguationData":[OSD([sQuery(id+"F0.wireOp",EDGE,"E0")])]})])],"derivedFrom":makeQuery(id+"F20.opExtrude","SWEPT_FACE",FACE,{"disambiguationData":[OSD([subQ2])]})});}
            var sketch = newSketch(context, id + "F21", { "sketchPlane" : qUnion([Q0])});
            skLineSegment(sketch, "E20", {"start": v(-62.5, -228.74) * mm, "end": v(69.52, -213.51) * mm});
            skLineSegment(sketch, "E21", {"start": v(69.52, -213.51) * mm, "end": v(69.52, -208.58) * mm});
            skLineSegment(sketch, "E22", {"start": v(69.52, -208.58) * mm, "end": v(-62.5, -223.82) * mm});
            skLineSegment(sketch, "E23", {"start": v(-62.5, -223.82) * mm, "end": v(-62.5, -228.74) * mm});
            skSolve(sketch);
        }
        {
            var Q0;
            {var subQ0=sQuery(id+"F21.wireOp",EDGE,"E21");Q0=makeQuery(id+"F21.imprint","IMPRINT",FACE,{"disambiguationData":[TD([[makeQuery(id+"F21.imprint","IMPRINT",EDGE,{"derivedFrom":subQ0}),1.0]])]});}
            var Q1;
            {var subQ0=sQuery(id+"F21.wireOp",EDGE,"E23");Q1=makeQuery(id+"F21.imprint","IMPRINT",FACE,{"disambiguationData":[TD([[makeQuery(id+"F21.imprint","IMPRINT",EDGE,{"derivedFrom":subQ0}),-1.0]])]});}
            extrude(context, id + "F22", {"entities" : qUnion([Q0, Q1]), "operationType" : NewBodyOperationType.ADD, "depth" : 5 * mm, "offsetDistance" : 25 * mm, "hasSecondDirection" : true, "secondDirectionOppositeDirection" : true, "secondDirectionDepth" : 130 * mm});
        }
        {
            var Q0;
            {var subQ1=sQuery(id+"F19.wireOp",EDGE,"E19.right");Q0=makeQuery(id+"F22.boolean.opBoolean","MERGE",FACE,{"derivedFrom":[makeQuery(id+"F20.boolean.opBoolean","SPLIT",FACE,{"disambiguationData":[TD([makeQuery(id+"F1.opExtrude","SWEPT_FACE",FACE,{"disambiguationData":[OSD([sQuery(id+"F0.wireOp",EDGE,"E0")])]})])],"derivedFrom":makeQuery(id+"F20.opExtrude","SWEPT_FACE",FACE,{"disambiguationData":[OSD([subQ1])]})}),makeQuery(id+"F22.opExtrude","SWEPT_FACE",FACE,{"disambiguationData":[OSD([sQuery(id+"F21.wireOp",EDGE,"E23")])]})]});}
            var sketch = newSketch(context, id + "F23", { "sketchPlane" : qUnion([Q0])});
            skCircle(sketch, "E24", {"center": v(-95, -199.22) * mm, "radius": 20 * mm});
            skCircle(sketch, "E25", {"center": v(-150, -199.22) * mm, "radius": 20 * mm});
            skSolve(sketch);
        }
        {
            var Q0;
            Q0 = qSketchRegion(id + "F23", true);
            extrude(context, id + "F24", {"entities" : qUnion([Q0]), "operationType" : NewBodyOperationType.ADD, "depth" : 5 * mm, "offsetDistance" : 25 * mm});
        }
        {
            var Q0;
            Q0=makeQuery(id+"F24.opExtrude","CAP_EDGE",EDGE,{"disambiguationData":[OSD([sQuery(id+"F23.wireOp",EDGE,"E24")])],"isStart":false});
            var Q1;
            Q1=makeQuery(id+"F24.opExtrude","CAP_EDGE",EDGE,{"disambiguationData":[OSD([sQuery(id+"F23.wireOp",EDGE,"E25")])],"isStart":false});
            fillet(context, id + "F25", {"entities" : qUnion([Q0, Q1]), "radius" : 5 * mm, "tangentPropagation" : true, "allowEdgeOverflow" : false});
        }
        {
            var Q0;
            Q0=makeQuery(id+"F20.opExtrude","CAP_EDGE",EDGE,{"disambiguationData":[OSD([sQuery(id+"F19.wireOp",EDGE,"E19.right")])],"isStart":false});
            var Q1;
            Q1=makeQuery(id+"F20.opExtrude","CAP_EDGE",EDGE,{"disambiguationData":[OSD([sQuery(id+"F19.wireOp",EDGE,"E19.bottom")])],"isStart":false});
            var Q2;
            Q2=makeQuery(id+"F20.opExtrude","CAP_EDGE",EDGE,{"disambiguationData":[OSD([sQuery(id+"F19.wireOp",EDGE,"E19.left")])],"isStart":false});
            var Q3;
            Q3=makeQuery(id+"F20.opExtrude","CAP_EDGE",EDGE,{"disambiguationData":[OSD([sQuery(id+"F19.wireOp",EDGE,"E19.top")])],"isStart":false});
            fillet(context, id + "F26", {"entities" : qUnion([Q0, Q1, Q2, Q3]), "radius" : 5 * mm, "tangentPropagation" : true, "allowEdgeOverflow" : false});
        }
        {
            var Q0;
            Q0=makeQuery(id+"F22.opExtrude","CAP_FACE",FACE,{"disambiguationData":[OSD([sQuery(id+"F21.wireOp",EDGE,"E20"),sQuery(id+"F21.wireOp",EDGE,"E21"),sQuery(id+"F21.wireOp",EDGE,"E22"),sQuery(id+"F21.wireOp",EDGE,"E23")])],"isStart":false});
            var Q1;
            Q1=makeQuery(id+"F22.opExtrude","SWEPT_FACE",FACE,{"disambiguationData":[OSD([sQuery(id+"F21.wireOp",EDGE,"E21")])]});
            var Q2;
            Q2=makeQuery(id+"F22.opExtrude","CAP_FACE",FACE,{"disambiguationData":[OSD([sQuery(id+"F21.wireOp",EDGE,"E20"),sQuery(id+"F21.wireOp",EDGE,"E21"),sQuery(id+"F21.wireOp",EDGE,"E22"),sQuery(id+"F21.wireOp",EDGE,"E23")])],"isStart":true});
            fillet(context, id + "F27", {"entities" : qUnion([Q0, Q1, Q2]), "radius" : 1 * mm, "tangentPropagation" : true, "allowEdgeOverflow" : false});
        }
        {
            var Q0;
            {var subQ0=sQuery(id+"F19.wireOp",EDGE,"E19.right");var subQ2=makeQuery(id+"F1.opExtrude","SWEPT_FACE",FACE,{"disambiguationData":[OSD([sQuery(id+"F0.wireOp",EDGE,"E0")])]});var subQ3=sQuery(id+"F19.wireOp",EDGE,"E19.bottom");Q0=makeQuery(id+"F22.boolean.opBoolean","SPLIT",EDGE,{"disambiguationData":[TD([subQ2])],"derivedFrom":makeQuery(id+"F20.boolean.opBoolean","SPLIT",EDGE,{"disambiguationData":[TD([subQ2])],"derivedFrom":makeQuery(id+"F20.opExtrude","SWEPT_EDGE",EDGE,{"disambiguationData":[OSD([subQ3,subQ0])]})})});}
            var Q1;
            {var subQ0=sQuery(id+"F19.wireOp",EDGE,"E19.right");var subQ2=sQuery(id+"F19.wireOp",EDGE,"E19.bottom");Q1=makeQuery(id+"F22.boolean.opBoolean","SPLIT",EDGE,{"disambiguationData":[TD([makeQuery(id+"F22.opExtrude","SWEPT_FACE",FACE,{"disambiguationData":[OSD([sQuery(id+"F21.wireOp",EDGE,"E20")])]})])],"derivedFrom":makeQuery(id+"F20.boolean.opBoolean","SPLIT",EDGE,{"disambiguationData":[TD([makeQuery(id+"F1.opExtrude","SWEPT_FACE",FACE,{"disambiguationData":[OSD([sQuery(id+"F0.wireOp",EDGE,"E0")])]})])],"derivedFrom":makeQuery(id+"F20.opExtrude","SWEPT_EDGE",EDGE,{"disambiguationData":[OSD([subQ2,subQ0])]})})});}
            var Q2;
            {var subQ0=sQuery(id+"F19.wireOp",EDGE,"E19.top");var subQ2=sQuery(id+"F19.wireOp",EDGE,"E19.right");var subQ4=makeQuery(id+"F1.opExtrude","SWEPT_FACE",FACE,{"disambiguationData":[OSD([sQuery(id+"F0.wireOp",EDGE,"E0")])]});Q2=makeQuery(id+"F22.boolean.opBoolean","SPLIT",EDGE,{"disambiguationData":[TD([subQ4])],"derivedFrom":makeQuery(id+"F20.boolean.opBoolean","SPLIT",EDGE,{"disambiguationData":[TD([subQ4])],"derivedFrom":makeQuery(id+"F20.opExtrude","SWEPT_EDGE",EDGE,{"disambiguationData":[OSD([subQ0,subQ2])]})})});}
            var Q3;
            {var subQ0=sQuery(id+"F19.wireOp",EDGE,"E19.right");var subQ2=sQuery(id+"F19.wireOp",EDGE,"E19.top");Q3=makeQuery(id+"F22.boolean.opBoolean","SPLIT",EDGE,{"disambiguationData":[TD([makeQuery(id+"F22.opExtrude","SWEPT_FACE",FACE,{"disambiguationData":[OSD([sQuery(id+"F21.wireOp",EDGE,"E20")])]})])],"derivedFrom":makeQuery(id+"F20.boolean.opBoolean","SPLIT",EDGE,{"disambiguationData":[TD([makeQuery(id+"F1.opExtrude","SWEPT_FACE",FACE,{"disambiguationData":[OSD([sQuery(id+"F0.wireOp",EDGE,"E0")])]})])],"derivedFrom":makeQuery(id+"F20.opExtrude","SWEPT_EDGE",EDGE,{"disambiguationData":[OSD([subQ2,subQ0])]})})});}
            var Q4;
            {var subQ0=makeQuery(id+"F1.opExtrude","SWEPT_FACE",FACE,{"disambiguationData":[OSD([sQuery(id+"F0.wireOp",EDGE,"E0")])]});var subQ1=sQuery(id+"F19.wireOp",EDGE,"E19.top");var subQ3=sQuery(id+"F19.wireOp",EDGE,"E19.left");Q4=makeQuery(id+"F22.boolean.opBoolean","SPLIT",EDGE,{"disambiguationData":[TD([subQ0])],"derivedFrom":makeQuery(id+"F20.boolean.opBoolean","SPLIT",EDGE,{"disambiguationData":[TD([subQ0])],"derivedFrom":makeQuery(id+"F20.opExtrude","SWEPT_EDGE",EDGE,{"disambiguationData":[OSD([subQ1,subQ3])]})})});}
            var Q5;
            {var subQ0=sQuery(id+"F19.wireOp",EDGE,"E19.left");var subQ1=sQuery(id+"F19.wireOp",EDGE,"E19.top");Q5=makeQuery(id+"F22.boolean.opBoolean","SPLIT",EDGE,{"disambiguationData":[TD([makeQuery(id+"F22.opExtrude","SWEPT_FACE",FACE,{"disambiguationData":[OSD([sQuery(id+"F21.wireOp",EDGE,"E20")])]})])],"derivedFrom":makeQuery(id+"F20.boolean.opBoolean","SPLIT",EDGE,{"disambiguationData":[TD([makeQuery(id+"F1.opExtrude","SWEPT_FACE",FACE,{"disambiguationData":[OSD([sQuery(id+"F0.wireOp",EDGE,"E0")])]})])],"derivedFrom":makeQuery(id+"F20.opExtrude","SWEPT_EDGE",EDGE,{"disambiguationData":[OSD([subQ1,subQ0])]})})});}
            var Q6;
            {var subQ0=makeQuery(id+"F1.opExtrude","SWEPT_FACE",FACE,{"disambiguationData":[OSD([sQuery(id+"F0.wireOp",EDGE,"E0")])]});var subQ1=sQuery(id+"F19.wireOp",EDGE,"E19.bottom");var subQ3=sQuery(id+"F19.wireOp",EDGE,"E19.left");Q6=makeQuery(id+"F22.boolean.opBoolean","SPLIT",EDGE,{"disambiguationData":[TD([subQ0])],"derivedFrom":makeQuery(id+"F20.boolean.opBoolean","SPLIT",EDGE,{"disambiguationData":[TD([subQ0])],"derivedFrom":makeQuery(id+"F20.opExtrude","SWEPT_EDGE",EDGE,{"disambiguationData":[OSD([subQ1,subQ3])]})})});}
            var Q7;
            {var subQ0=sQuery(id+"F19.wireOp",EDGE,"E19.bottom");var subQ2=sQuery(id+"F19.wireOp",EDGE,"E19.left");Q7=makeQuery(id+"F22.boolean.opBoolean","SPLIT",EDGE,{"disambiguationData":[TD([makeQuery(id+"F22.opExtrude","SWEPT_FACE",FACE,{"disambiguationData":[OSD([sQuery(id+"F21.wireOp",EDGE,"E20")])]})])],"derivedFrom":makeQuery(id+"F20.boolean.opBoolean","SPLIT",EDGE,{"disambiguationData":[TD([makeQuery(id+"F1.opExtrude","SWEPT_FACE",FACE,{"disambiguationData":[OSD([sQuery(id+"F0.wireOp",EDGE,"E0")])]})])],"derivedFrom":makeQuery(id+"F20.opExtrude","SWEPT_EDGE",EDGE,{"disambiguationData":[OSD([subQ0,subQ2])]})})});}
            fillet(context, id + "F28", {"entities" : qUnion([Q0, Q1, Q2, Q3, Q4, Q5, Q6, Q7]), "radius" : 2 * mm, "tangentPropagation" : true, "allowEdgeOverflow" : false});
        }
        {
            var Q0;
            Q0=qCreatedBy(makeId("Top.planeOp"),FACE);
            var sketch = newSketch(context, id + "F29", { "sketchPlane" : qUnion([Q0])});
            skCircle(sketch, "E26", {"center": v(0, -265) * mm, "radius": 10 * mm});
            skSolve(sketch);
        }
        {
            var Q0;
            Q0 = qSketchRegion(id + "F29", true);
            var Q1;
            Q1=sQuery(id+"F29.wireOp",EDGE,"E26");
            extrude(context, id + "F30", {"entities" : qUnion([Q0]), "operationType" : NewBodyOperationType.ADD, "surfaceEntities" : qUnion([Q1]), "oppositeDirection" : true, "depth" : 160 * mm, "offsetDistance" : 25 * mm});
        }
        {
            var Q0;
            Q0=qCreatedBy(makeId("Right.planeOp"),FACE);
            var sketch = newSketch(context, id + "F31", { "sketchPlane" : qUnion([Q0])});
            skCircle(sketch, "E27", {"center": v(-265, -182) * mm, "radius": 25 * mm});
            skLineSegment(sketch, "E28", {"start": v(-275, -160) * mm, "end": v(-275, -145) * mm});
            skCircle(sketch, "E29", {"center": v(-265, -182) * mm, "radius": 15 * mm});
            skSolve(sketch);
        }
        {
            var Q0;
            Q0=makeQuery(id+"F31.imprint","IMPRINT",FACE,{"disambiguationData":[TD([[makeQuery(id+"F31.imprint","IMPRINT",EDGE,{"derivedFrom":sQuery(id+"F31.wireOp",EDGE,"E27")}),1.0]])]});
            extrude(context, id + "F32", {"entities" : qUnion([Q0]), "operationType" : NewBodyOperationType.ADD, "endBound" : BoundingType.SYMMETRIC, "depth" : 10 * mm, "offsetDistance" : 25 * mm});
        }
        {
            var Q0;
            Q0=makeQuery(id+"F32.opExtrude","CAP_EDGE",EDGE,{"disambiguationData":[OSD([sQuery(id+"F31.wireOp",EDGE,"E27")])],"isStart":false});
            var Q1;
            Q1=makeQuery(id+"F32.opExtrude","CAP_EDGE",EDGE,{"disambiguationData":[OSD([sQuery(id+"F31.wireOp",EDGE,"E27")])],"isStart":true});
            var Q2;
            Q2=makeQuery(id+"F32.opExtrude","CAP_EDGE",EDGE,{"disambiguationData":[OSD([sQuery(id+"F31.wireOp",EDGE,"E29")])],"isStart":false});
            var Q3;
            Q3=makeQuery(id+"F32.opExtrude","CAP_EDGE",EDGE,{"disambiguationData":[OSD([sQuery(id+"F31.wireOp",EDGE,"E29")])],"isStart":true});
            fillet(context, id + "F33", {"entities" : qUnion([Q0, Q1, Q2, Q3]), "radius" : 5 * mm, "tangentPropagation" : true, "allowEdgeOverflow" : false});
        }
        {
            var Q0;
            Q0=makeQuery(id+"F32.boolean.opBoolean","INTERSECT",EDGE,{"derivedFrom":[makeQuery(id+"F30.opExtrude","CAP_FACE",FACE,{"disambiguationData":[OSD([sQuery(id+"F29.wireOp",EDGE,"E26")])],"isStart":false}),makeQuery(id+"F32.opExtrude","CAP_FACE",FACE,{"disambiguationData":[OSD([sQuery(id+"F31.wireOp",EDGE,"E27"),sQuery(id+"F31.wireOp",EDGE,"E29")])],"isStart":false})]});
            var Q1;
            Q1=makeQuery(id+"F32.boolean.opBoolean","INTERSECT",EDGE,{"derivedFrom":[makeQuery(id+"F30.opExtrude","CAP_FACE",FACE,{"disambiguationData":[OSD([sQuery(id+"F29.wireOp",EDGE,"E26")])],"isStart":false}),makeQuery(id+"F32.opExtrude","CAP_FACE",FACE,{"disambiguationData":[OSD([sQuery(id+"F31.wireOp",EDGE,"E27"),sQuery(id+"F31.wireOp",EDGE,"E29")])],"isStart":true})]});
            fillet(context, id + "F34", {"entities" : qUnion([Q0, Q1]), "radius" : 5 * mm, "tangentPropagation" : true, "allowEdgeOverflow" : false});
        }
    });
